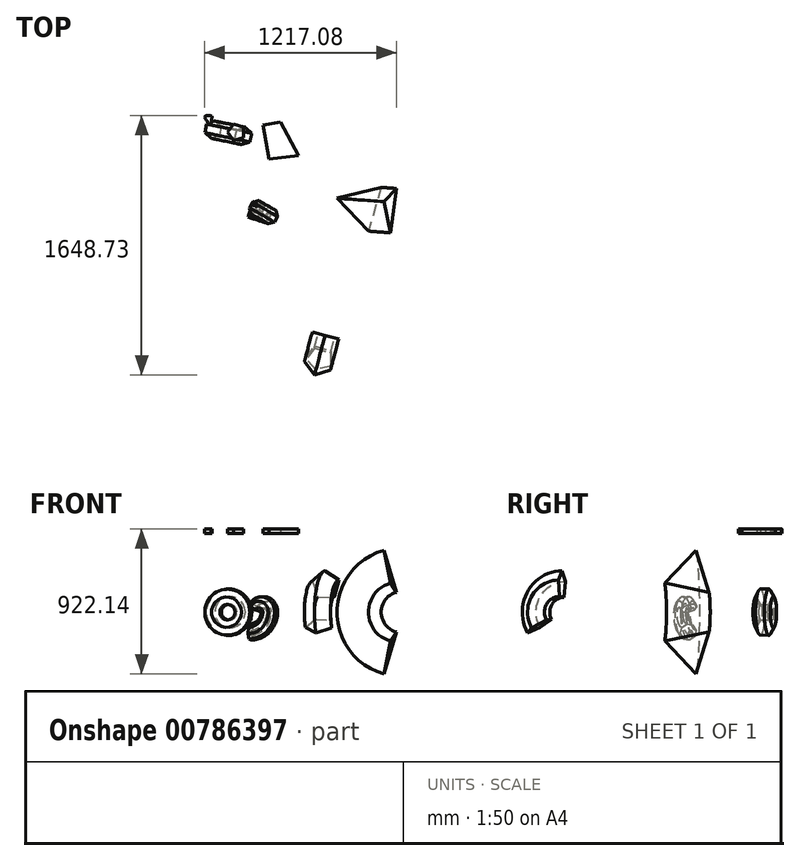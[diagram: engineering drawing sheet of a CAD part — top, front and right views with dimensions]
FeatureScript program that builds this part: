
annotation { "Feature Type Name" : "Feature", "Feature Type Description" : "" }
export const myFeature = defineFeature(function(context is Context, id is Id, definition is map)
    precondition{}
    {
        {
            var Q0;
            Q0=qCreatedBy(makeId("Top.planeOp"),FACE);
            var sketch = newSketch(context, id + "F0", { "sketchPlane" : qUnion([Q0])});
            skCircle(sketch, "E0.cCircle", {"center": v(0, 0) * mm, "radius": 48.68 * mm, "construction": true});
            skLineSegment(sketch, "E0.0", {"start": v(53.75, 16.45) * mm, "end": v(41.12, -38.33) * mm});
            skLineSegment(sketch, "E0.1", {"start": v(41.12, -38.33) * mm, "end": v(-12.63, -54.78) * mm});
            skLineSegment(sketch, "E0.2", {"start": v(-12.63, -54.78) * mm, "end": v(-53.75, -16.45) * mm});
            skLineSegment(sketch, "E0.3", {"start": v(-53.75, -16.45) * mm, "end": v(-41.12, 38.33) * mm});
            skLineSegment(sketch, "E0.4", {"start": v(-41.12, 38.33) * mm, "end": v(12.63, 54.78) * mm});
            skLineSegment(sketch, "E0.5", {"start": v(12.63, 54.78) * mm, "end": v(53.75, 16.45) * mm});
            skPoint(sketch, "E0.0.midPoint", {"position": v(47.44, -10.94) * mm});
            skSolve(sketch);
        }
        {
            var Q0;
            Q0=qCreatedBy(makeId("Top.planeOp"),FACE);
            var sketch = newSketch(context, id + "F1", { "sketchPlane" : qUnion([Q0])});
            skLineSegment(sketch, "E1", {"start": v(-121.98, -107.17) * mm, "end": v(-80.14, 97.44) * mm});
            skSolve(sketch);
        }
        {
            var Q0;
            Q0=makeQuery(id+"F0.imprint","IMPRINT",FACE,{"disambiguationData":[TD([[makeQuery(id+"F0.imprint","IMPRINT",EDGE,{"derivedFrom":sQuery(id+"F0.wireOp",EDGE,"E0.0")}),-1.0]])]});
            var Q1;
            Q1=sQuery(id+"F1.wireOp",EDGE,"E1");
            revolve(context, id + "F2", {"surfaceOperationType" : NewSurfaceOperationType.NEW, "entities" : qUnion([Q0]), "axis" : qUnion([Q1]), "revolveType" : RevolveType.FULL});
        }
        {
            var Q0;
            Q0=qCreatedBy(makeId("Top.planeOp"),FACE);
            var sketch = newSketch(context, id + "F3", { "sketchPlane" : qUnion([Q0])});
            skCircle(sketch, "E2.cCircle", {"center": v(165.13, -505.64) * mm, "radius": 48.7 * mm, "construction": true});
            skLineSegment(sketch, "E2.0", {"start": v(217.43, -512.2) * mm, "end": v(197.48, -547.26) * mm});
            skLineSegment(sketch, "E2.1", {"start": v(197.48, -547.26) * mm, "end": v(158.58, -557.94) * mm});
            skLineSegment(sketch, "E2.2", {"start": v(158.58, -557.94) * mm, "end": v(123.52, -537.99) * mm});
            skLineSegment(sketch, "E2.3", {"start": v(123.52, -537.99) * mm, "end": v(112.83, -499.09) * mm});
            skLineSegment(sketch, "E2.4", {"start": v(112.83, -499.09) * mm, "end": v(132.79, -464.03) * mm});
            skLineSegment(sketch, "E2.5", {"start": v(132.79, -464.03) * mm, "end": v(171.69, -453.34) * mm});
            skLineSegment(sketch, "E2.6", {"start": v(171.69, -453.34) * mm, "end": v(206.75, -473.3) * mm});
            skLineSegment(sketch, "E2.7", {"start": v(206.75, -473.3) * mm, "end": v(217.43, -512.2) * mm});
            skPoint(sketch, "E2.0.midPoint", {"position": v(207.46, -529.72) * mm});
            skLineSegment(sketch, "E3", {"start": v(8.65, -577.96) * mm, "end": v(58.24, -427.34) * mm});
            skSolve(sketch);
        }
        {
            var Q0;
            Q0=makeQuery(id+"F3.imprint","IMPRINT",FACE,{"disambiguationData":[TD([[makeQuery(id+"F3.imprint","IMPRINT",EDGE,{"derivedFrom":sQuery(id+"F3.wireOp",EDGE,"E2.0")}),-1.0]])]});
            var Q1;
            Q1=sQuery(id+"F3.wireOp",EDGE,"E3");
            revolve(context, id + "F4", {"surfaceOperationType" : NewSurfaceOperationType.NEW, "entities" : qUnion([Q0]), "axis" : qUnion([Q1]), "revolveType" : RevolveType.ONE_DIRECTION, "angle" : 90 * degree});
        }
        {
            var Q0;
            Q0=makeQuery(id+"F4.opRevolve","CAP_FACE",FACE,{"disambiguationData":[OSD([sQuery(id+"F3.wireOp",EDGE,"E2.0"),sQuery(id+"F3.wireOp",EDGE,"E2.1"),sQuery(id+"F3.wireOp",EDGE,"E2.2"),sQuery(id+"F3.wireOp",EDGE,"E2.3"),sQuery(id+"F3.wireOp",EDGE,"E2.4"),sQuery(id+"F3.wireOp",EDGE,"E2.5"),sQuery(id+"F3.wireOp",EDGE,"E2.6"),sQuery(id+"F3.wireOp",EDGE,"E2.7")])],"isStart":true});
            var sketch = newSketch(context, id + "F5", { "sketchPlane" : qUnion([Q0])});
            skCircle(sketch, "E4", {"center": v(161.72, -498.3) * mm, "radius": 14.64 * mm});
            skLineSegment(sketch, "E5", {"start": v(-55.28, -669.66) * mm, "end": v(60.97, -395.28) * mm});
            skSolve(sketch);
        }
        {
            var Q0;
            Q0=makeQuery(id+"F5.imprint","IMPRINT",FACE,{"disambiguationData":[TD([[makeQuery(id+"F5.imprint","IMPRINT",EDGE,{"derivedFrom":sQuery(id+"F5.wireOp",EDGE,"E4")}),1.0]])]});
            var Q1;
            Q1=sQuery(id+"F5.wireOp",EDGE,"E5");
            revolve(context, id + "F6", {"operationType" : NewBodyOperationType.REMOVE, "surfaceOperationType" : NewSurfaceOperationType.NEW, "entities" : qUnion([Q0]), "axis" : qUnion([Q1]), "revolveType" : RevolveType.ONE_DIRECTION, "angle" : 90 * degree});
        }
        {
            var Q0;
            Q0=makeQuery(id+"F4.opRevolve","CAP_FACE",FACE,{"disambiguationData":[OSD([sQuery(id+"F3.wireOp",EDGE,"E2.0"),sQuery(id+"F3.wireOp",EDGE,"E2.1"),sQuery(id+"F3.wireOp",EDGE,"E2.2"),sQuery(id+"F3.wireOp",EDGE,"E2.3"),sQuery(id+"F3.wireOp",EDGE,"E2.4"),sQuery(id+"F3.wireOp",EDGE,"E2.5"),sQuery(id+"F3.wireOp",EDGE,"E2.6"),sQuery(id+"F3.wireOp",EDGE,"E2.7")])],"isStart":true});
            var Q1;
            Q1=makeQuery(id+"F4.opRevolve","CAP_EDGE",EDGE,{"disambiguationData":[OSD([sQuery(id+"F3.wireOp",EDGE,"E2.4")])],"isStart":true});
            revolve(context, id + "F7", {"operationType" : NewBodyOperationType.ADD, "surfaceOperationType" : NewSurfaceOperationType.NEW, "entities" : qUnion([Q0]), "axis" : qUnion([Q1]), "revolveType" : RevolveType.ONE_DIRECTION, "oppositeDirection" : true, "angle" : 150 * degree});
        }
        {
            var Q0;
            Q0=qCreatedBy(makeId("Top.planeOp"),FACE);
            var sketch = newSketch(context, id + "F8", { "sketchPlane" : qUnion([Q0])});
            skCircle(sketch, "E6.cCircle", {"center": v(754.55, -442.47) * mm, "radius": 83.63 * mm, "construction": true});
            skLineSegment(sketch, "E6.0", {"start": v(875.38, -326.82) * mm, "end": v(794.29, -604.93) * mm});
            skLineSegment(sketch, "E6.1", {"start": v(794.29, -604.93) * mm, "end": v(593.98, -395.65) * mm});
            skLineSegment(sketch, "E6.2", {"start": v(593.98, -395.65) * mm, "end": v(875.38, -326.82) * mm});
            skPoint(sketch, "E6.0.midPoint", {"position": v(834.83, -465.88) * mm});
            skLineSegment(sketch, "E7", {"start": v(982.83, -639.32) * mm, "end": v(1016.01, -196.56) * mm});
            skSolve(sketch);
        }
        {
            var Q0;
            Q0=makeQuery(id+"F8.imprint","IMPRINT",FACE,{"disambiguationData":[TD([[makeQuery(id+"F8.imprint","IMPRINT",EDGE,{"derivedFrom":sQuery(id+"F8.wireOp",EDGE,"E6.0")}),-1.0]])]});
            var Q1;
            Q1=sQuery(id+"F8.wireOp",EDGE,"E7");
            revolve(context, id + "F9", {"surfaceOperationType" : NewSurfaceOperationType.NEW, "entities" : qUnion([Q0]), "axis" : qUnion([Q1]), "revolveType" : RevolveType.SYMMETRIC, "angle" : 150 * degree});
        }
        {
            var Q0;
            Q0=qCreatedBy(makeId("Top.planeOp"),FACE);
            var sketch = newSketch(context, id + "F10", { "sketchPlane" : qUnion([Q0])});
            skCircle(sketch, "E8.cCircle", {"center": v(479.38, -1432.92) * mm, "radius": 74.06 * mm, "construction": true});
            skLineSegment(sketch, "E8.0", {"start": v(553.44, -1379.11) * mm, "end": v(553.44, -1486.73) * mm});
            skLineSegment(sketch, "E8.1", {"start": v(553.44, -1486.73) * mm, "end": v(451.1, -1519.99) * mm});
            skLineSegment(sketch, "E8.2", {"start": v(451.1, -1519.99) * mm, "end": v(387.83, -1432.92) * mm});
            skLineSegment(sketch, "E8.3", {"start": v(387.83, -1432.92) * mm, "end": v(451.1, -1345.86) * mm});
            skLineSegment(sketch, "E8.4", {"start": v(451.1, -1345.86) * mm, "end": v(553.44, -1379.11) * mm});
            skPoint(sketch, "E8.0.midPoint", {"position": v(553.44, -1432.92) * mm});
            skLineSegment(sketch, "E9", {"start": v(286.7, -1204.68) * mm, "end": v(768.46, -1333.77) * mm});
            skSolve(sketch);
        }
        {
            var Q0;
            Q0=makeQuery(id+"F10.imprint","IMPRINT",FACE,{"disambiguationData":[TD([[makeQuery(id+"F10.imprint","IMPRINT",EDGE,{"derivedFrom":sQuery(id+"F10.wireOp",EDGE,"E8.0")}),-1.0]])]});
            var Q1;
            Q1=sQuery(id+"F10.wireOp",EDGE,"E9");
            revolve(context, id + "F11", {"surfaceOperationType" : NewSurfaceOperationType.NEW, "entities" : qUnion([Q0]), "axis" : qUnion([Q1]), "revolveType" : RevolveType.TWO_DIRECTIONS, "angle" : 30 * degree, "angleBack" : 270 * degree});
        }
        {
            var Q0;
            Q0=qCreatedBy(makeId("Top.planeOp"),FACE);
            cPlane(context, id + "F12", {"entities" : qUnion([Q0]), "cplaneType" : CPlaneType.OFFSET, "offset" : 500 * mm, "width" : 150 * mm, "height" : 150 * mm});
        }
        {
            var Q0;
            Q0=qCreatedBy(id+"F12.planeOp",FACE);
            var sketch = newSketch(context, id + "F13", { "sketchPlane" : qUnion([Q0])});
            skLineSegment(sketch, "E10", {"start": v(-231.2, -150.37) * mm, "end": v(-194.44, 169.43) * mm});
            skPoint(sketch, "E11.4.internal.snap0", {"position": v(-212.82, 9.53) * mm});
            skFitSpline(sketch, "E11", {"points": [v(-210.98, -147.18) * mm, v(-271.3, -63.26) * mm, v(-168.12, -93.6) * mm, v(-264.34, 28.98) * mm, v(-157.39, 9.53) * mm, v(-244.89, 121.64) * mm, v(-156.59, 120.03) * mm, v(-155.32, 120.76) * mm], "startDerivative": vector(-773.73, 813.07) * mm, "endDerivative": vector(10.46, 57.28) * mm});
            skCircle(sketch, "E12.cCircle", {"center": v(-44.81, 23.4) * mm, "radius": 44.81 * mm, "construction": true});
            skLineSegment(sketch, "E12.0", {"start": v(0, 55.96) * mm, "end": v(0, -9.16) * mm});
            skLineSegment(sketch, "E12.1", {"start": v(0, -9.16) * mm, "end": v(-61.93, -29.28) * mm});
            skLineSegment(sketch, "E12.2", {"start": v(-61.93, -29.28) * mm, "end": v(-100.2, 23.4) * mm});
            skLineSegment(sketch, "E12.3", {"start": v(-100.2, 23.4) * mm, "end": v(-61.93, 76.08) * mm});
            skLineSegment(sketch, "E12.4", {"start": v(-61.93, 76.08) * mm, "end": v(0, 55.96) * mm});
            skPoint(sketch, "E12.0.midPoint", {"position": v(0, 23.4) * mm});
            skLineSegment(sketch, "E13", {"start": v(173.9, -209.98) * mm, "end": v(123.64, 68.07) * mm});
            skLineSegment(sketch, "E14", {"start": v(123.64, 68.07) * mm, "end": v(237.14, 88.58) * mm});
            skLineSegment(sketch, "E15", {"start": v(237.14, 88.58) * mm, "end": v(404.69, -227.72) * mm});
            skLineSegment(sketch, "E16", {"start": v(107.95, -153.05) * mm, "end": v(392.37, -121.17) * mm});
            skLineSegment(sketch, "E17", {"start": v(-34.85, -372.91) * mm, "end": v(-103.15, -156.18) * mm});
            skLineSegment(sketch, "E18", {"start": v(-103.15, -156.18) * mm, "end": v(37.02, -265.26) * mm});
            skLineSegment(sketch, "E19", {"start": v(37.02, -265.26) * mm, "end": v(106.33, -422.04) * mm});
            skSolve(sketch);
        }
        {
            var Q0;
            {var subQ0=sQuery(id+"F13.wireOp",EDGE,"E11");var subQ1=sQuery(id+"F13.wireOp",EDGE,"E10");var subQ2=makeQuery(id+"F13.imprint","INTERSECT",VERTEX,{"disambiguationData":[OD(0.0)],"derivedFrom":[subQ1,subQ0]});Q0=makeQuery(id+"F13.imprint","IMPRINT",FACE,{"disambiguationData":[TD([[makeQuery(id+"F13.imprint","IMPRINT",EDGE,{"disambiguationData":[TD([[subQ2,-1.0]])],"derivedFrom":subQ1}),1.0]])]});}
            var Q1;
            {var subQ0=sQuery(id+"F13.wireOp",EDGE,"E11");var subQ1=sQuery(id+"F13.wireOp",EDGE,"E10");var subQ2=makeQuery(id+"F13.imprint","INTERSECT",VERTEX,{"disambiguationData":[OD(2.0)],"derivedFrom":[subQ1,subQ0]});Q1=makeQuery(id+"F13.imprint","IMPRINT",FACE,{"disambiguationData":[TD([[makeQuery(id+"F13.imprint","IMPRINT",EDGE,{"disambiguationData":[TD([[subQ2,-1.0]])],"derivedFrom":subQ1}),-1.0]])]});}
            var Q2;
            {var subQ0=sQuery(id+"F13.wireOp",EDGE,"E11");var subQ1=sQuery(id+"F13.wireOp",EDGE,"E10");var subQ2=makeQuery(id+"F13.imprint","INTERSECT",VERTEX,{"disambiguationData":[OD(3.0)],"derivedFrom":[subQ1,subQ0]});Q2=makeQuery(id+"F13.imprint","IMPRINT",FACE,{"disambiguationData":[TD([[makeQuery(id+"F13.imprint","IMPRINT",EDGE,{"disambiguationData":[TD([[subQ2,-1.0]])],"derivedFrom":subQ1}),1.0]])]});}
            var Q3;
            {var subQ0=sQuery(id+"F13.wireOp",EDGE,"E11");var subQ1=sQuery(id+"F13.wireOp",EDGE,"E10");var subQ2=makeQuery(id+"F13.imprint","INTERSECT",VERTEX,{"disambiguationData":[OD(1.0)],"derivedFrom":[subQ1,subQ0]});Q3=makeQuery(id+"F13.imprint","IMPRINT",FACE,{"disambiguationData":[TD([[makeQuery(id+"F13.imprint","IMPRINT",EDGE,{"disambiguationData":[TD([[subQ2,1.0]])],"derivedFrom":subQ1}),1.0]])]});}
            var Q4;
            {var subQ0=sQuery(id+"F13.wireOp",EDGE,"E11");var subQ1=sQuery(id+"F13.wireOp",EDGE,"E10");var subQ2=makeQuery(id+"F13.imprint","INTERSECT",VERTEX,{"disambiguationData":[OD(4.0)],"derivedFrom":[subQ1,subQ0]});Q4=makeQuery(id+"F13.imprint","IMPRINT",FACE,{"disambiguationData":[TD([[makeQuery(id+"F13.imprint","IMPRINT",EDGE,{"disambiguationData":[TD([[subQ2,-1.0]])],"derivedFrom":subQ1}),-1.0]])]});}
            var Q5;
            Q5=makeQuery(id+"F13.imprint","IMPRINT",FACE,{"disambiguationData":[TD([[makeQuery(id+"F13.imprint","IMPRINT",EDGE,{"derivedFrom":sQuery(id+"F13.wireOp",EDGE,"E12.0")}),-1.0]])]});
            var Q6;
            {var subQ0=sQuery(id+"F13.wireOp",EDGE,"E14");Q6=makeQuery(id+"F13.imprint","IMPRINT",FACE,{"disambiguationData":[TD([[makeQuery(id+"F13.imprint","IMPRINT",EDGE,{"derivedFrom":subQ0}),-1.0]])]});}
            var Q7;
            Q7=sQuery(id+"F13.wireOp",EDGE,"E18");
            var Q8;
            Q8=sQuery(id+"F13.wireOp",EDGE,"E19");
            var Q9;
            Q9=sQuery(id+"F13.wireOp",EDGE,"E17");
            var Q10;
            Q10=sQuery(id+"F13.wireOp",EDGE,"E13");
            var Q11;
            Q11=sQuery(id+"F13.wireOp",EDGE,"E12.4");
            var Q12;
            Q12=sQuery(id+"F13.wireOp",EDGE,"E10");
            var Q13;
            Q13=sQuery(id+"F13.wireOp",EDGE,"E12.3");
            var Q14;
            Q14=sQuery(id+"F13.wireOp",EDGE,"E12.2");
            var Q15;
            Q15=sQuery(id+"F13.wireOp",EDGE,"E11");
            var Q16;
            Q16=sQuery(id+"F13.wireOp",EDGE,"E12.1");
            var Q17;
            Q17=sQuery(id+"F13.wireOp",EDGE,"E12.0");
            var Q18;
            Q18=sQuery(id+"F13.wireOp",EDGE,"E15");
            var Q19;
            Q19=sQuery(id+"F13.wireOp",EDGE,"E16");
            var Q20;
            Q20=sQuery(id+"F13.wireOp",EDGE,"E14");
            extrude(context, id + "F14", {"entities" : qUnion([Q0, Q1, Q2, Q3, Q4, Q5, Q6]), "surfaceEntities" : qUnion([Q7, Q8, Q9, Q10, Q11, Q12, Q13, Q14, Q15, Q16, Q17, Q18, Q19, Q20]), "depth" : 30 * mm, "offsetDistance" : 25 * mm});
        }
    });
